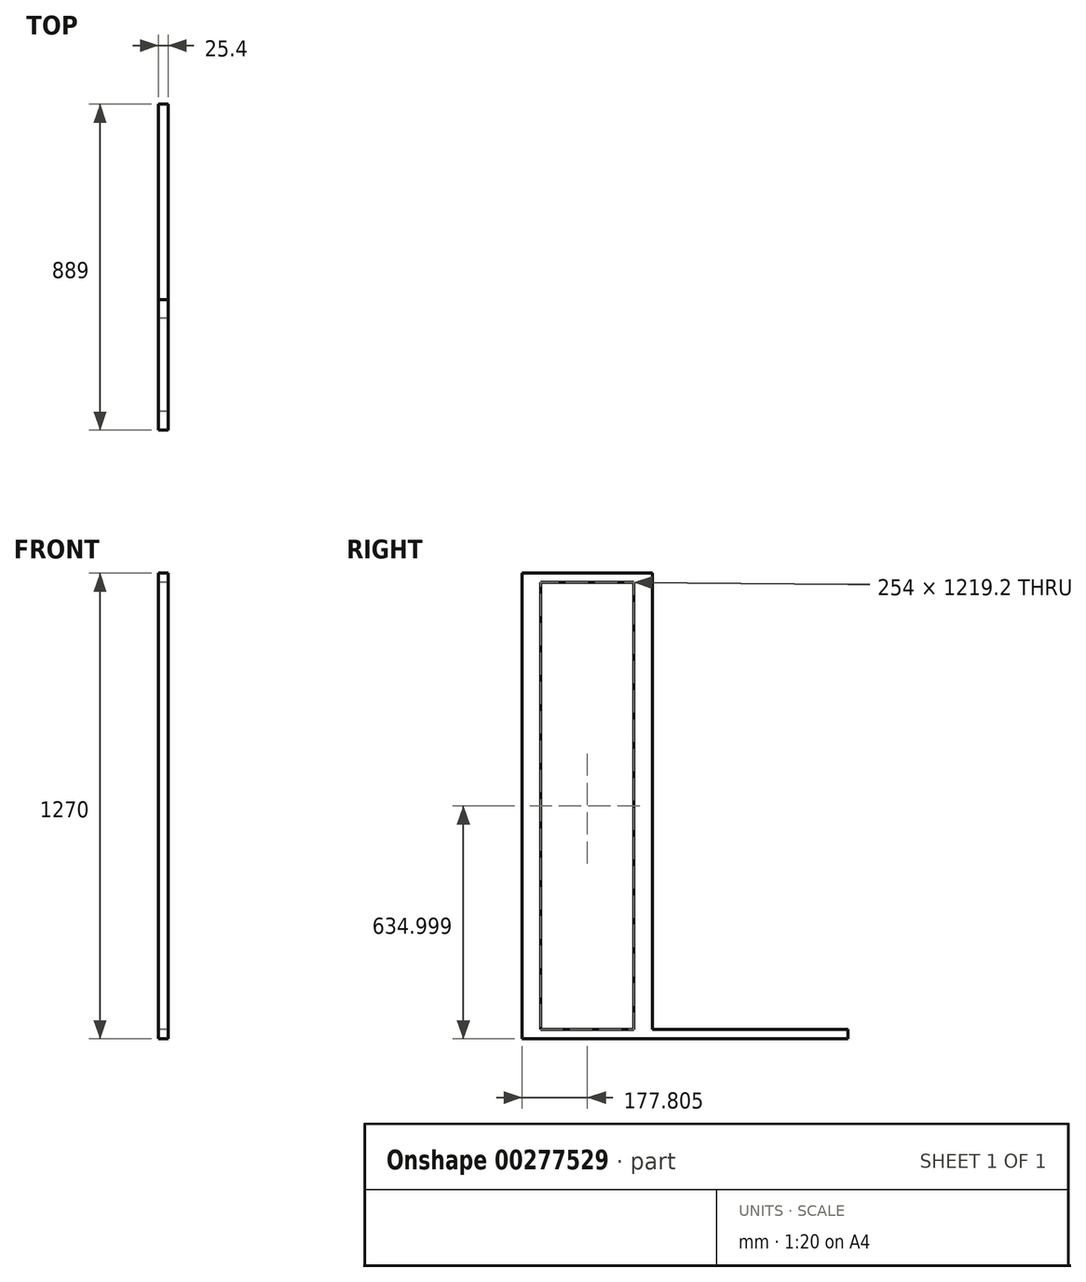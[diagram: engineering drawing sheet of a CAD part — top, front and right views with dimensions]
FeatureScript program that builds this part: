
annotation { "Feature Type Name" : "Feature", "Feature Type Description" : "" }
export const myFeature = defineFeature(function(context is Context, id is Id, definition is map)
    precondition{}
    {
        {
            var Q0;
            Q0=qCreatedBy(makeId("Right.planeOp"),FACE);
            var sketch = newSketch(context, id + "F0", { "sketchPlane" : qUnion([Q0])});
            skLineSegment(sketch, "E0.bottom", {"start": v(350.8, -336.32) * mm, "end": v(-538.2, -336.32) * mm});
            skLineSegment(sketch, "E0.top", {"start": v(350.8, -361.72) * mm, "end": v(-538.2, -361.72) * mm});
            skLineSegment(sketch, "E0.left", {"start": v(350.8, -336.32) * mm, "end": v(350.8, -361.72) * mm});
            skLineSegment(sketch, "E0.right", {"start": v(-538.2, -336.32) * mm, "end": v(-538.2, -361.72) * mm});
            skLineSegment(sketch, "E1.bottom", {"start": v(-233.4, -336.32) * mm, "end": v(-182.6, -336.32) * mm});
            skLineSegment(sketch, "E1.top", {"start": v(-233.4, 882.88) * mm, "end": v(-182.6, 882.88) * mm});
            skLineSegment(sketch, "E1.left", {"start": v(-233.4, -336.32) * mm, "end": v(-233.4, 882.88) * mm});
            skLineSegment(sketch, "E1.right", {"start": v(-182.6, -336.32) * mm, "end": v(-182.6, 882.88) * mm});
            skLineSegment(sketch, "E2.bottom", {"start": v(-538.2, -336.32) * mm, "end": v(-487.4, -336.32) * mm});
            skLineSegment(sketch, "E2.top", {"start": v(-538.2, 882.88) * mm, "end": v(-487.4, 882.88) * mm});
            skLineSegment(sketch, "E2.left", {"start": v(-538.2, -336.32) * mm, "end": v(-538.2, 882.88) * mm});
            skLineSegment(sketch, "E2.right", {"start": v(-487.4, -336.32) * mm, "end": v(-487.4, 882.88) * mm});
            skLineSegment(sketch, "E3.bottom", {"start": v(-538.2, 882.88) * mm, "end": v(-182.6, 882.88) * mm});
            skLineSegment(sketch, "E3.top", {"start": v(-538.2, 908.28) * mm, "end": v(-182.6, 908.28) * mm});
            skLineSegment(sketch, "E3.left", {"start": v(-538.2, 882.88) * mm, "end": v(-538.2, 908.28) * mm});
            skLineSegment(sketch, "E3.right", {"start": v(-182.6, 882.88) * mm, "end": v(-182.6, 908.28) * mm});
            skSolve(sketch);
        }
        {
            var Q0;
            Q0 = qSketchRegion(id + "F0", true);
            extrude(context, id + "F1", {"entities" : qUnion([Q0]), "depth" : 25.4 * mm});
        }
    });
